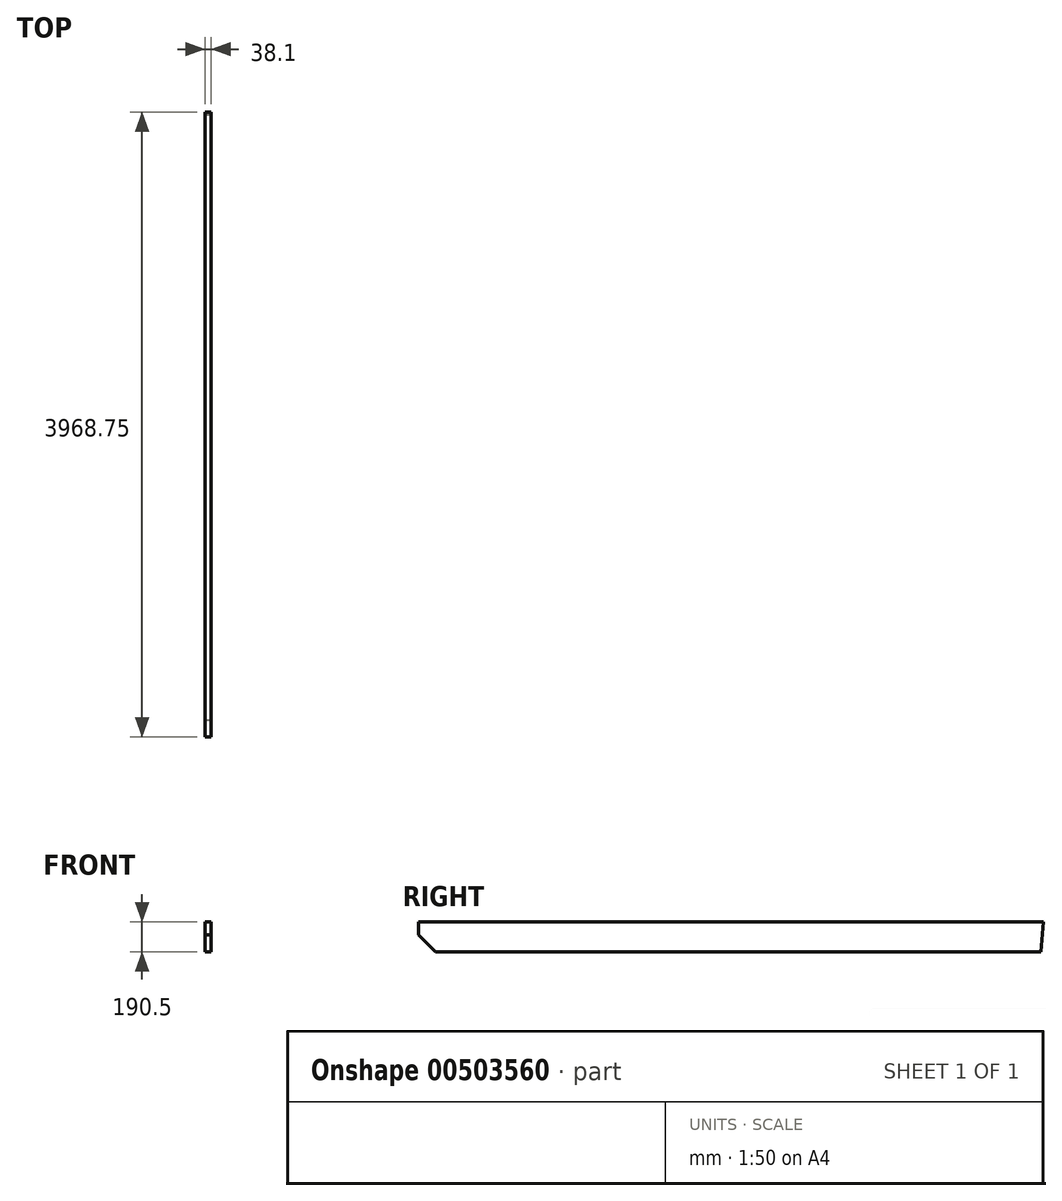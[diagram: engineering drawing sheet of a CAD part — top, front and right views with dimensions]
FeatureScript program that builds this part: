
annotation { "Feature Type Name" : "Feature", "Feature Type Description" : "" }
export const myFeature = defineFeature(function(context is Context, id is Id, definition is map)
    precondition{}
    {
        {
            var Q0;
            Q0=qCreatedBy(makeId("Front.planeOp"),FACE);
            var sketch = newSketch(context, id + "F0", { "sketchPlane" : qUnion([Q0])});
            skLineSegment(sketch, "E0.bottom", {"start": v(0, 0) * mm, "end": v(38.1, 0) * mm});
            skLineSegment(sketch, "E0.top", {"start": v(0, 190.5) * mm, "end": v(38.1, 190.5) * mm});
            skLineSegment(sketch, "E0.left", {"start": v(0, 0) * mm, "end": v(0, 190.5) * mm});
            skLineSegment(sketch, "E0.right", {"start": v(38.1, 0) * mm, "end": v(38.1, 190.5) * mm});
            skSolve(sketch);
        }
        {
            var Q0;
            Q0 = qSketchRegion(id + "F0", true);
            extrude(context, id + "F1", {"entities" : qUnion([Q0]), "depth" : 4267.2 * mm});
        }
        {
            var Q0;
            Q0=makeQuery(id+"F1.opExtrude","SWEPT_FACE",FACE,{"disambiguationData":[OSD([sQuery(id+"F0.wireOp",EDGE,"E0.right")])]});
            var sketch = newSketch(context, id + "F2", { "sketchPlane" : qUnion([Q0])});
            skLineSegment(sketch, "E1", {"start": v(0, 190.5) * mm, "end": v(-16.26, 0) * mm});
            skLineSegment(sketch, "E2", {"start": v(-16.26, 0) * mm, "end": v(0, 0) * mm});
            skLineSegment(sketch, "E3", {"start": v(0, 0) * mm, "end": v(0, 190.5) * mm});
            skSolve(sketch);
        }
        {
            var Q0;
            Q0 = qSketchRegion(id + "F2", true);
            extrude(context, id + "F3", {"entities" : qUnion([Q0]), "operationType" : NewBodyOperationType.REMOVE, "endBound" : BoundingType.THROUGH_ALL, "oppositeDirection" : true, "depth" : 25.4 * mm});
        }
        {
            var Q0;
            Q0=makeQuery(id+"F1.opExtrude","SWEPT_FACE",FACE,{"disambiguationData":[OSD([sQuery(id+"F0.wireOp",EDGE,"E0.right")])]});
            var sketch = newSketch(context, id + "F4", { "sketchPlane" : qUnion([Q0])});
            skLineSegment(sketch, "E4", {"start": v(-3968.75, 190.5) * mm, "end": v(-3968.75, 107.95) * mm});
            skLineSegment(sketch, "E5", {"start": v(-3968.75, 107.95) * mm, "end": v(-3860.8, 0) * mm});
            skLineSegment(sketch, "E6", {"start": v(-3968.75, 190.5) * mm, "end": v(-4267.2, 190.5) * mm});
            skLineSegment(sketch, "E7", {"start": v(-4267.2, 190.5) * mm, "end": v(-4267.2, 0) * mm});
            skLineSegment(sketch, "E8", {"start": v(-4267.2, 0) * mm, "end": v(-3860.8, 0) * mm});
            skSolve(sketch);
        }
        {
            var Q0;
            Q0 = qSketchRegion(id + "F4", true);
            extrude(context, id + "F5", {"entities" : qUnion([Q0]), "operationType" : NewBodyOperationType.REMOVE, "endBound" : BoundingType.THROUGH_ALL, "oppositeDirection" : true, "depth" : 25.4 * mm});
        }
    });
